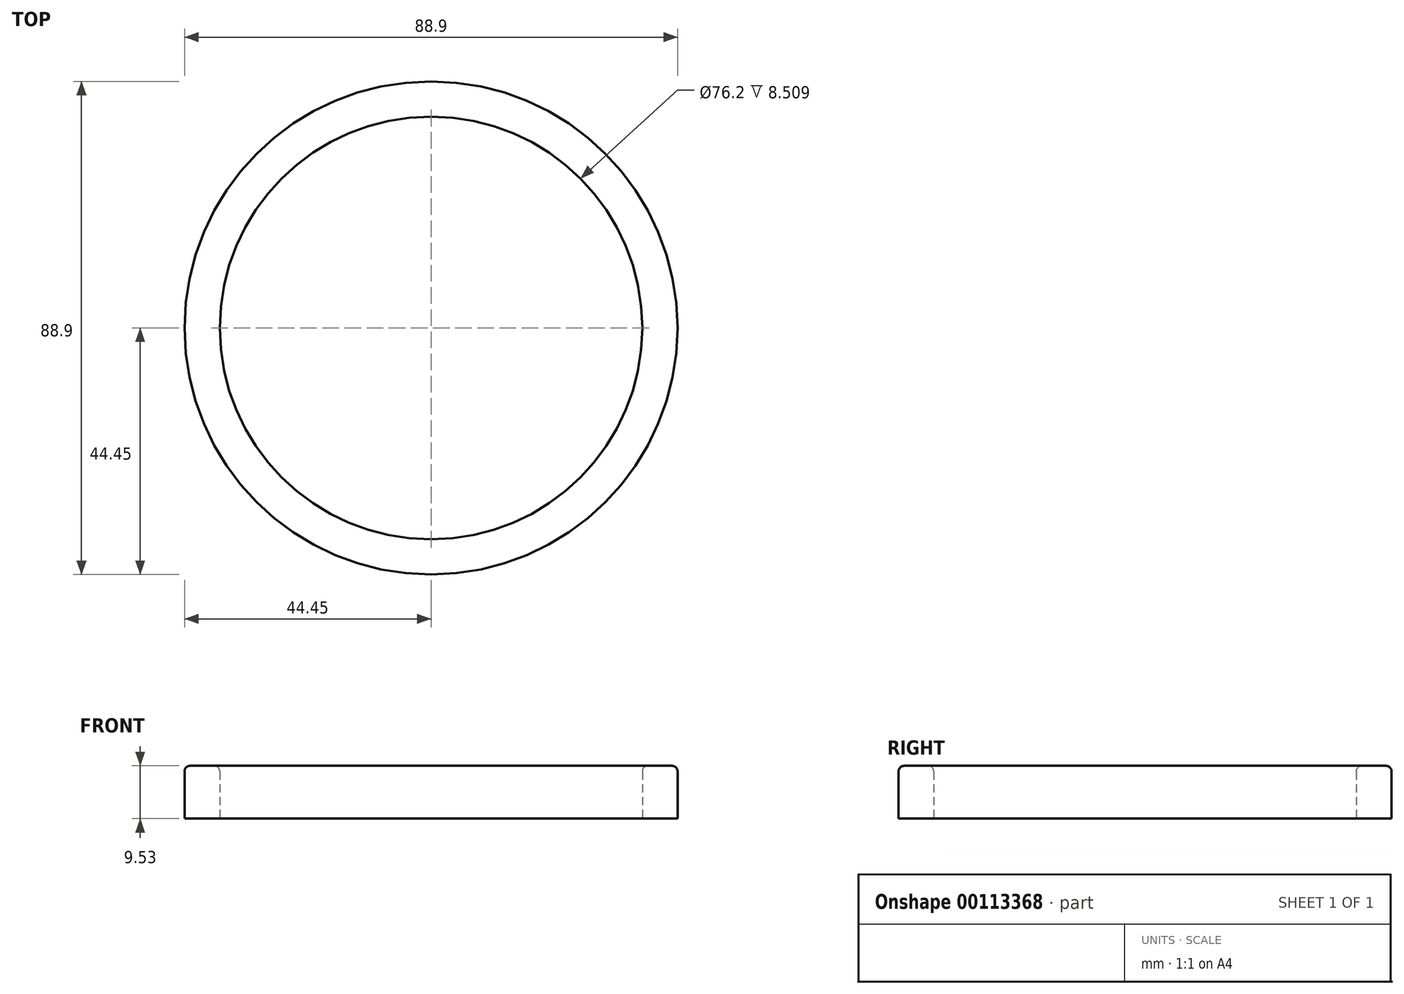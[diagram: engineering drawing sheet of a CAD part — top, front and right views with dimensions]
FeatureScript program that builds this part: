
annotation { "Feature Type Name" : "Feature", "Feature Type Description" : "" }
export const myFeature = defineFeature(function(context is Context, id is Id, definition is map)
    precondition{}
    {
        {
            var Q0;
            Q0=qCreatedBy(makeId("Top.planeOp"),FACE);
            var sketch = newSketch(context, id + "F0", { "sketchPlane" : qUnion([Q0])});
            skCircle(sketch, "E0", {"center": v(0, 0) * mm, "radius": 38.1 * mm});
            skCircle(sketch, "E1", {"center": v(0, 0) * mm, "radius": 44.45 * mm});
            skSolve(sketch);
        }
        {
            var Q0;
            Q0 = qSketchRegion(id + "F0", true);
            extrude(context, id + "F1", {"entities" : qUnion([Q0]), "depth" : 9.52 * mm, "offsetDistance" : 25.4 * mm});
        }
        {
            var Q0;
            Q0=makeQuery(id+"F1.opExtrude","CAP_EDGE",EDGE,{"disambiguationData":[OSD([sQuery(id+"F0.wireOp",EDGE,"E1")])],"isStart":false});
            var Q1;
            Q1=makeQuery(id+"F1.opExtrude","CAP_EDGE",EDGE,{"disambiguationData":[OSD([sQuery(id+"F0.wireOp",EDGE,"E0")])],"isStart":false});
            fillet(context, id + "F2", {"entities" : qUnion([Q0, Q1]), "tangentPropagation" : true, "radius" : 1.02 * mm, "defaultsChanged" : false, "vertexSettings" : [], "allowEdgeOverflow" : false});
        }
    });
